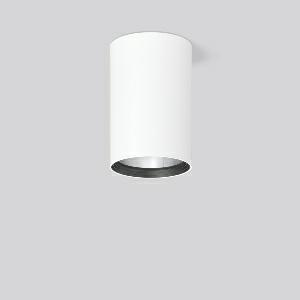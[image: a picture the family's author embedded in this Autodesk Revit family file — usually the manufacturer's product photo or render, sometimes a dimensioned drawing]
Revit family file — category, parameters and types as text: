
# Revit family: heledon_maxi_a_931230_002_8a33
name_source: partatom
category: Lighting Fixtures
units: mm (PartAtom-declared; Revit-internal decimal feet)

## family parameters
Cut with Voids When Loaded = No
Host = Face
Light Source = No
Part Type = Normal
Room Calculation Point = No
Round Connector Dimension = Use Diameter
Shared = No

## types (1)
- HELEDON maxi A (1 x LED Modul 932 fresh meat, 2100 lm, 3200)
    Apparent Load = 33 VA
    Approval mark = CE
    CIE Flux Codes = 100 100 100 100 100
    Color Rendering = 90
    Color Temperature = 3200
    Default Elevation = 1800 mm
    Description = Series: HELEDON maxi
Cylindrical surface-mounted downlight. Housing: die-cast aluminium, powder-coated. Internal ceiling frame polycarbonate with bayonet mounting. Black plastic ring and recessed LED to prevent glare from the side. Optical assembly with reflector made of MIRO-Silver with 98% total light reflection for outstanding efficiency - can be changed without tools. Special LED for illumination of meat included. Suitable for Ceiling mounting. Easy installation with a separate ceiling frame with bayonet mounting and plug connection. Driver integrated. Connected via plug-in connector. High quality converter without flickering and stroboscopic effect. The following accessories can be mounted without use of tools: interchangeable lenses, decorative glasses, honeycomb louvre, clear and frosted diffusers, white interchangeable plastic ring. 
Colour: traffic white, matt (RAL 9016)
Diameter: 123 mm
Height: 183 mm
Lamp: LED
Socket: without socket
Colour temperature: fresh meat
System power: 33 W
Rated luminous flux: 2100 lm
Luminous efficiency: 64 lm/W
Control gear: Regulated power supply
Protection class: I
Type of protection: IP 20
    Height = 183 mm
    Lamp = 1 x LED Modul 932 fresh meat
    Lamp Light Flux = 2100 lm
    Lamp count = 1
    Length = 123 mm
    Lifetime = 50000 h
    Luminous efficacy = 64 lm/W
    Manufacturer = RZB
    ModVariant = No
    Model = 931230.002
    Mounting Place = Ceiling
    Mounting Type = Surface mounted
    Number of Poles = 1
    OnlyDefault = Yes
    Power Factor = 1
    Product Name = HELEDON maxi A
    Product group = Surface mounted downlights
    ProductGroupID = 302
    Protection Class = Protection class I
    Protection Degree = IP 20
    RLX_Detail_Level = 1
    RLX_Emergency_Light_Flux = 0 lm
    RLX_Emergency_Type = 0
    RLX_Emergency_Type_DB = No
    RlxData = <blob elided: 96445 chars, md5=5adc74f4>
    Socket = socket
    Standby Power = 0 W
    System Light Flux = 2100 lm
    System Power = 33 W
    Type Comments = Product without accessories
    Type Image = 931192.002.jpg
    URL = http://relux.com
    VarID = ---
    Voltage = 230 V
    Voltage Range = 220-240 V
    Weight = 0.00 kg
    Width = 0 mm  [stored 0 ft]

note: [stored X ft] marks values corroborated as IEEE doubles in the binary element streams (Revit-internal decimal feet)

## geometry (parser evidence)
native form markers: Blend x4, Sweep x9
no freeform markers — native parametric forms only
